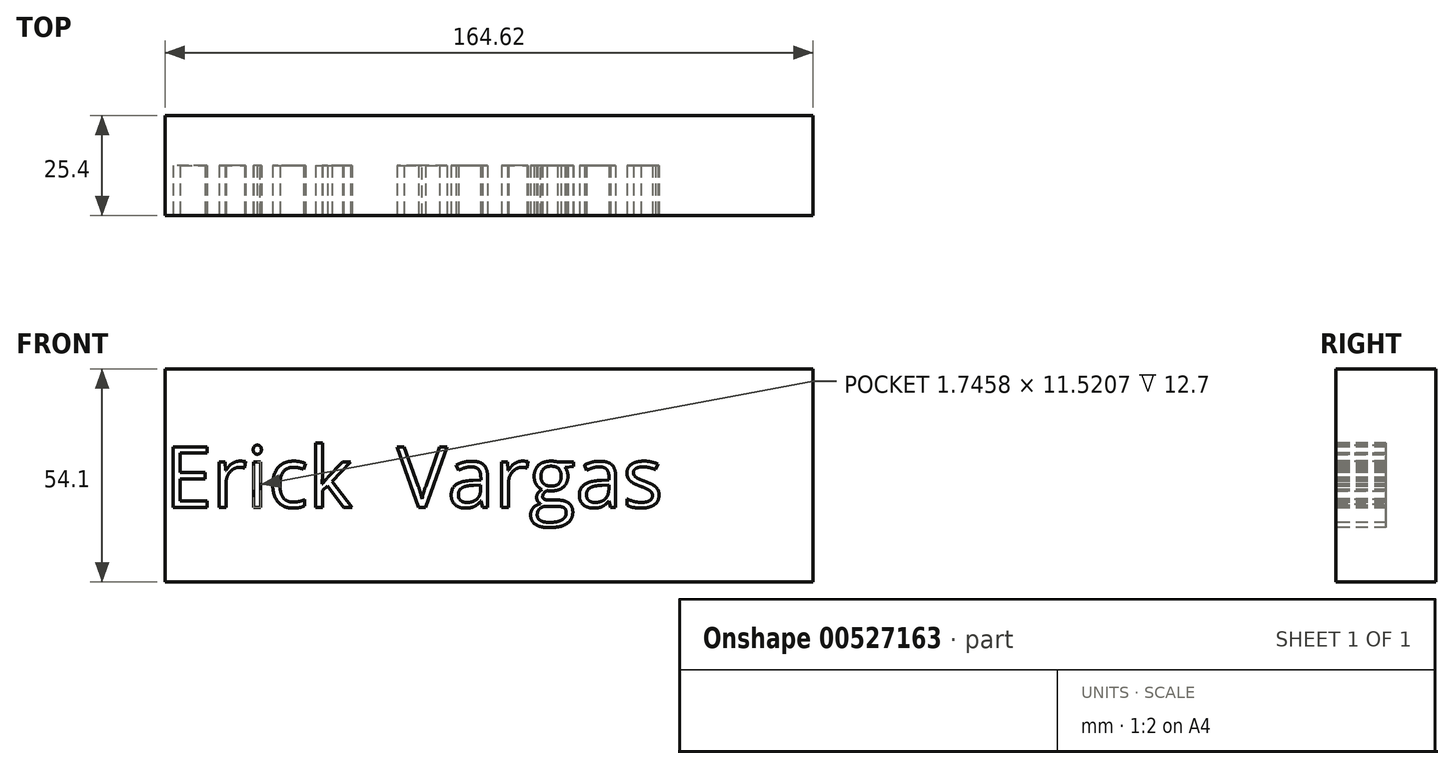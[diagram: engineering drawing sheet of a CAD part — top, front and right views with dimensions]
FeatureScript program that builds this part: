
annotation { "Feature Type Name" : "Feature", "Feature Type Description" : "" }
export const myFeature = defineFeature(function(context is Context, id is Id, definition is map)
    precondition{}
    {
        {
            var Q0;
            Q0=qCreatedBy(makeId("Front.planeOp"),FACE);
            var sketch = newSketch(context, id + "F0", { "sketchPlane" : qUnion([Q0])});
            skLineSegment(sketch, "E0.bottom", {"start": v(82.31, 27.05) * mm, "end": v(-82.31, 27.05) * mm});
            skLineSegment(sketch, "E0.top", {"start": v(82.31, -27.05) * mm, "end": v(-82.31, -27.05) * mm});
            skLineSegment(sketch, "E0.left", {"start": v(82.31, 27.05) * mm, "end": v(82.31, -27.05) * mm});
            skLineSegment(sketch, "E0.right", {"start": v(-82.31, 27.05) * mm, "end": v(-82.31, -27.05) * mm});
            skPoint(sketch, "E0.middle", {"position": v(0, 0) * mm});
            skSolve(sketch);
        }
        {
            var Q0;
            Q0 = qSketchRegion(id + "F0", true);
            extrude(context, id + "F1", {"entities" : qUnion([Q0]), "depth" : 25.4 * mm, "offsetDistance" : 25.4 * mm});
        }
        {
            var Q0;
            Q0=makeQuery(id+"F1.opExtrude","CAP_FACE",FACE,{"disambiguationData":[OSD([sQuery(id+"F0.wireOp",EDGE,"E0.bottom"),sQuery(id+"F0.wireOp",EDGE,"E0.top"),sQuery(id+"F0.wireOp",EDGE,"E0.left"),sQuery(id+"F0.wireOp",EDGE,"E0.right")])],"isStart":false});
            var sketch = newSketch(context, id + "F2", { "sketchPlane" : qUnion([Q0])});
            skText(sketch, "E1", { "text": "Erick  Vargas", "fontName": "OpenSans-Regular.ttf"});
            const initialGuessF2  = {"E1": [-0.08235, -0.00808, 1, 0, 0.0155]};
            skSetInitialGuess(sketch, initialGuessF2);
            skSolve(sketch);
        }
        {
            var Q0;
            Q0 = qSketchRegion(id + "F2", true);
            extrude(context, id + "F3", {"entities" : qUnion([Q0]), "operationType" : NewBodyOperationType.REMOVE, "oppositeDirection" : true, "depth" : 12.7 * mm, "offsetDistance" : 25.4 * mm});
        }
    });
